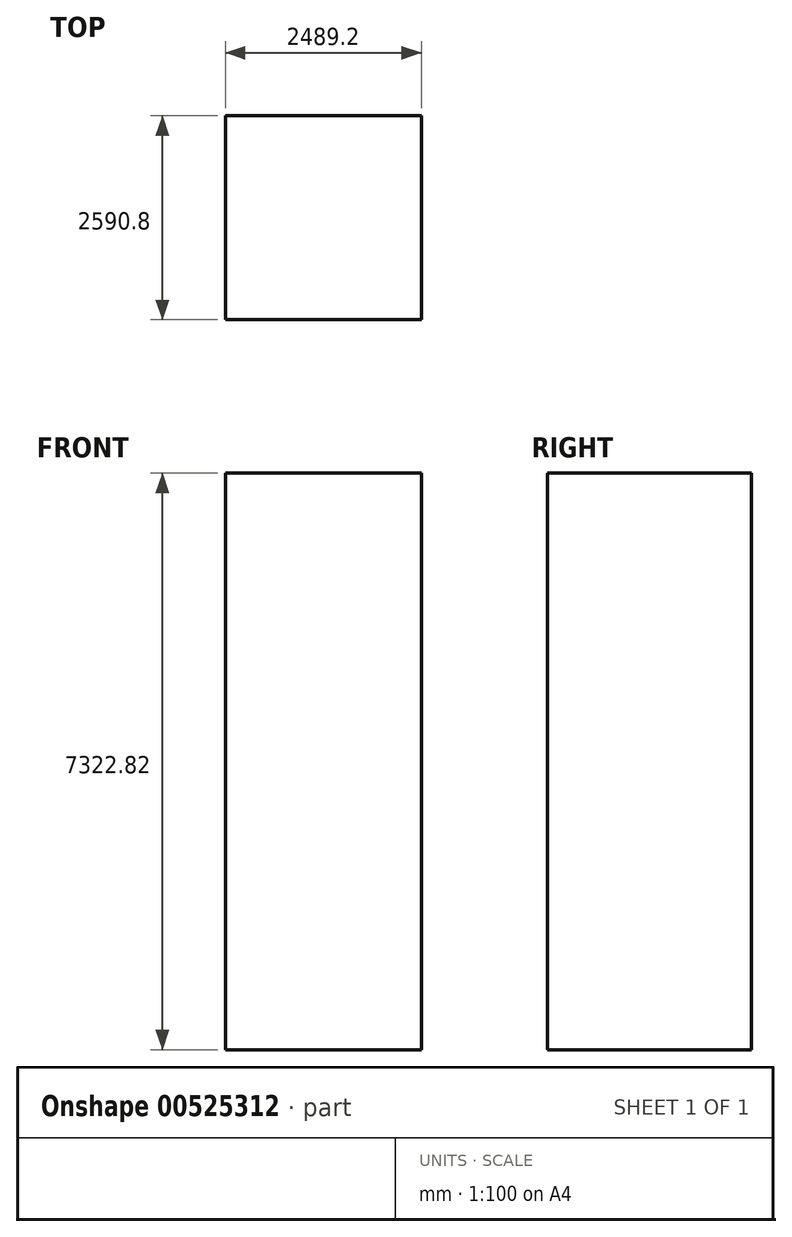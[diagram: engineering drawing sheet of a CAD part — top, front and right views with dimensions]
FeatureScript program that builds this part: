
annotation { "Feature Type Name" : "Feature", "Feature Type Description" : "" }
export const myFeature = defineFeature(function(context is Context, id is Id, definition is map)
    precondition{}
    {
        {
            var Q0;
            Q0=qCreatedBy(makeId("Top.planeOp"),FACE);
            var sketch = newSketch(context, id + "F0", { "sketchPlane" : qUnion([Q0])});
            skLineSegment(sketch, "E0.bottom", {"start": v(0, 0) * mm, "end": v(2489.2, 0) * mm});
            skLineSegment(sketch, "E0.top", {"start": v(0, 2590.8) * mm, "end": v(2489.2, 2590.8) * mm});
            skLineSegment(sketch, "E0.left", {"start": v(0, 0) * mm, "end": v(0, 2590.8) * mm});
            skLineSegment(sketch, "E0.right", {"start": v(2489.2, 0) * mm, "end": v(2489.2, 2590.8) * mm});
            skSolve(sketch);
        }
        {
            var Q0;
            Q0 = qSketchRegion(id + "F0", true);
            extrude(context, id + "F1", {"entities" : qUnion([Q0]), "depth" : 7322.82 * mm, "offsetDistance" : 25.4 * mm});
        }
    });
